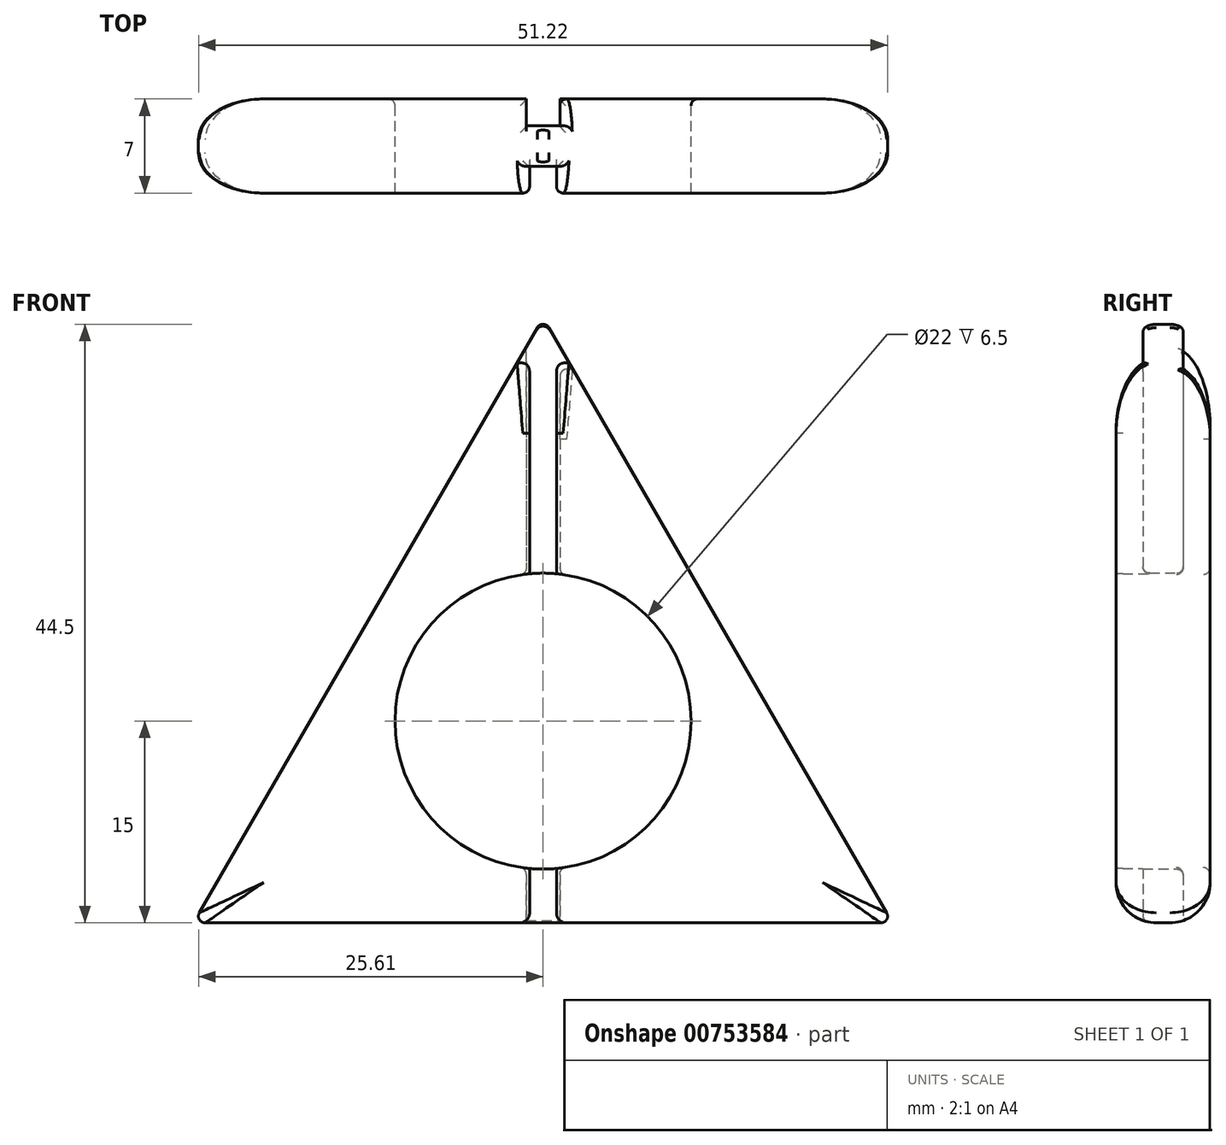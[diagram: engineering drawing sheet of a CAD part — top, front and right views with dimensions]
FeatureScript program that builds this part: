
annotation { "Feature Type Name" : "Feature", "Feature Type Description" : "" }
export const myFeature = defineFeature(function(context is Context, id is Id, definition is map)
    precondition{}
    {
        {
            var Q0;
            Q0=qCreatedBy(makeId("Front.planeOp"),FACE);
            var sketch = newSketch(context, id + "F0", { "sketchPlane" : qUnion([Q0])});
            skPoint(sketch, "E0.center", {"position": v(0, 0) * mm});
            skLineSegment(sketch, "E1", {"start": v(0, 30) * mm, "end": v(-25.98, -15) * mm});
            skLineSegment(sketch, "E2", {"start": v(25.98, -15) * mm, "end": v(-25.98, -15) * mm});
            skLineSegment(sketch, "E3", {"start": v(25.98, -15) * mm, "end": v(0, 30) * mm});
            skCircle(sketch, "E4", {"center": v(0, 0) * mm, "radius": 11 * mm});
            skLineSegment(sketch, "E5", {"start": v(0, 11) * mm, "end": v(0, 30) * mm});
            skSolve(sketch);
        }
        {
            var Q0;
            Q0=makeQuery(id+"F0.imprint","IMPRINT",FACE,{"disambiguationData":[TD([[makeQuery(id+"F0.imprint","IMPRINT",EDGE,{"derivedFrom":sQuery(id+"F0.wireOp",EDGE,"E1")}),1.0]])]});
            extrude(context, id + "F1", {"entities" : qUnion([Q0]), "depth" : 7 * mm, "offsetDistance" : 25.4 * mm});
        }
        {
            var Q0;
            Q0=qCreatedBy(makeId("Front.planeOp"),FACE);
            var sketch = newSketch(context, id + "F2", { "sketchPlane" : qUnion([Q0])});
            skLineSegment(sketch, "E6", {"start": v(-1.25, 30.57) * mm, "end": v(-1.25, 19.34) * mm});
            skLineSegment(sketch, "E7", {"start": v(-1.25, 36.4) * mm, "end": v(-1.25, 9.77) * mm});
            skLineSegment(sketch, "E8.MirrorCS", {"start": v(1.25, 36.4) * mm, "end": v(1.25, 9.77) * mm});
            skLineSegment(sketch, "E9", {"start": v(-1.25, 36.4) * mm, "end": v(1.25, 36.4) * mm});
            skLineSegment(sketch, "E10", {"start": v(-1.25, 9.77) * mm, "end": v(1.25, 9.77) * mm});
            skArc(sketch, "E11", {"start": v(1.25, 10.92) * mm, "mid": v(0, 11) * mm, "end": v(-1.25, 10.92) * mm});
            skLineSegment(sketch, "E12", {"start": v(-1.25, 27.85) * mm, "end": v(0, 30) * mm});
            skLineSegment(sketch, "E13", {"start": v(0, 30) * mm, "end": v(1.25, 27.84) * mm});
            skLineSegment(sketch, "E14", {"start": v(1.25, -10.91) * mm, "end": v(1.25, -15) * mm});
            skLineSegment(sketch, "E15.MirrorCS", {"start": v(-1.25, -10.91) * mm, "end": v(-1.25, -15) * mm});
            skLineSegment(sketch, "E16", {"start": v(1.25, -15) * mm, "end": v(-1.25, -15) * mm});
            skLineSegment(sketch, "E17", {"start": v(1.25, -10.91) * mm, "end": v(-1.25, -10.91) * mm});
            skSolve(sketch);
        }
        {
            var Q0;
            Q0 = qSketchRegion(id + "F2", true);
            extrude(context, id + "F3", {"entities" : qUnion([Q0]), "operationType" : NewBodyOperationType.REMOVE, "oppositeDirection" : true, "depth" : -2 * mm, "offsetDistance" : 25.4 * mm});
        }
        {
            var Q0;
            Q0=makeQuery(id+"F1.opExtrude","CAP_EDGE",EDGE,{"disambiguationData":[OSD([sQuery(id+"F0.wireOp",EDGE,"E3")])],"isStart":true});
            var Q1;
            Q1=makeQuery(id+"F1.opExtrude","CAP_EDGE",EDGE,{"disambiguationData":[OSD([sQuery(id+"F0.wireOp",EDGE,"E3")])],"isStart":false});
            var Q2;
            Q2=makeQuery(id+"F1.opExtrude","CAP_EDGE",EDGE,{"disambiguationData":[OSD([sQuery(id+"F0.wireOp",EDGE,"E1")])],"isStart":true});
            var Q3;
            {var subQ0=sQuery(id+"F0.wireOp",EDGE,"E1");var subQ1=sQuery(id+"F0.wireOp",EDGE,"E2");Q3=makeQuery(id+"F3.boolean.opBoolean","SPLIT",EDGE,{"disambiguationData":[TD([makeQuery(id+"F1.opExtrude","SWEPT_FACE",FACE,{"disambiguationData":[OSD([subQ0])]})])],"derivedFrom":makeQuery(id+"F1.opExtrude","CAP_EDGE",EDGE,{"disambiguationData":[OSD([subQ1])],"isStart":true})});}
            var Q4;
            Q4=makeQuery(id+"F1.opExtrude","CAP_EDGE",EDGE,{"disambiguationData":[OSD([sQuery(id+"F0.wireOp",EDGE,"E2")])],"isStart":false});
            var Q5;
            {var subQ0=sQuery(id+"F0.wireOp",EDGE,"E3");var subQ1=sQuery(id+"F0.wireOp",EDGE,"E2");Q5=makeQuery(id+"F3.boolean.opBoolean","SPLIT",EDGE,{"disambiguationData":[TD([makeQuery(id+"F1.opExtrude","SWEPT_FACE",FACE,{"disambiguationData":[OSD([subQ0])]})])],"derivedFrom":makeQuery(id+"F1.opExtrude","CAP_EDGE",EDGE,{"disambiguationData":[OSD([subQ1])],"isStart":true})});}
            var Q6;
            Q6=makeQuery(id+"F1.opExtrude","CAP_EDGE",EDGE,{"disambiguationData":[OSD([sQuery(id+"F0.wireOp",EDGE,"E1")])],"isStart":false});
            fillet(context, id + "F4", {"entities" : qUnion([Q0, Q1, Q2, Q3, Q4, Q5, Q6]), "radius" : 3 * mm, "tangentPropagation" : true, "allowEdgeOverflow" : false});
        }
        {
            var Q0;
            {var subQ0=sQuery(id+"F0.wireOp",EDGE,"E4");Q0=makeQuery(id+"F3.boolean.opBoolean","SPLIT",EDGE,{"disambiguationData":[TD([makeQuery(id+"F3.opExtrude","SWEPT_FACE",FACE,{"disambiguationData":[OSD([sQuery(id+"F2.wireOp",EDGE,"E7")])]})])],"derivedFrom":makeQuery(id+"F1.opExtrude","CAP_EDGE",EDGE,{"disambiguationData":[OSD([subQ0])],"isStart":true})});}
            var Q1;
            {var subQ0=sQuery(id+"F0.wireOp",EDGE,"E4");Q1=makeQuery(id+"F3.boolean.opBoolean","SPLIT",EDGE,{"disambiguationData":[TD([makeQuery(id+"F3.opExtrude","SWEPT_FACE",FACE,{"disambiguationData":[OSD([sQuery(id+"F2.wireOp",EDGE,"E8.MirrorCS")])]})])],"derivedFrom":makeQuery(id+"F1.opExtrude","CAP_EDGE",EDGE,{"disambiguationData":[OSD([subQ0])],"isStart":true})});}
            var Q2;
            Q2=makeQuery(id+"F3.boolean.opBoolean","INTERSECT",EDGE,{"derivedFrom":[makeQuery(id+"F1.opExtrude","SWEPT_FACE",FACE,{"disambiguationData":[OSD([sQuery(id+"F0.wireOp",EDGE,"E4")])]}),makeQuery(id+"F3.opExtrude","SWEPT_FACE",FACE,{"disambiguationData":[OSD([sQuery(id+"F2.wireOp",EDGE,"E15.MirrorCS")])]})]});
            var Q3;
            Q3=makeQuery(id+"F3.boolean.opBoolean","INTERSECT",EDGE,{"derivedFrom":[makeQuery(id+"F1.opExtrude","SWEPT_FACE",FACE,{"disambiguationData":[OSD([sQuery(id+"F0.wireOp",EDGE,"E4")])]}),makeQuery(id+"F3.opExtrude","SWEPT_FACE",FACE,{"disambiguationData":[OSD([sQuery(id+"F2.wireOp",EDGE,"E14")])]})]});
            var Q4;
            Q4=makeQuery(id+"F3.boolean.opBoolean","INTERSECT",EDGE,{"derivedFrom":[makeQuery(id+"F1.opExtrude","SWEPT_FACE",FACE,{"disambiguationData":[OSD([sQuery(id+"F0.wireOp",EDGE,"E4")])]}),makeQuery(id+"F3.opExtrude","CAP_FACE",FACE,{"disambiguationData":[OSD([sQuery(id+"F2.wireOp",EDGE,"E14"),sQuery(id+"F2.wireOp",EDGE,"E15.MirrorCS"),sQuery(id+"F2.wireOp",EDGE,"E16"),sQuery(id+"F2.wireOp",EDGE,"E17")])],"isStart":false})]});
            var Q5;
            {var subQ0=sQuery(id+"F2.wireOp",EDGE,"E14");var subQ1=sQuery(id+"F0.wireOp",EDGE,"E3");var subQ2=sQuery(id+"F0.wireOp",EDGE,"E2");Q5=makeQuery(id+"F4.opFillet","BLEND_EDGE",EDGE,{"blendedFrom":[makeQuery(id+"F3.boolean.opBoolean","SPLIT",EDGE,{"disambiguationData":[TD([makeQuery(id+"F1.opExtrude","SWEPT_FACE",FACE,{"disambiguationData":[OSD([subQ1])]})])],"derivedFrom":makeQuery(id+"F1.opExtrude","CAP_EDGE",EDGE,{"disambiguationData":[OSD([subQ2])],"isStart":true})}),makeQuery(id+"F3.boolean.opBoolean","COPY",FACE,{"derivedFrom":makeQuery(id+"F3.opExtrude","CAP_FACE",FACE,{"disambiguationData":[OSD([subQ0,sQuery(id+"F2.wireOp",EDGE,"E15.MirrorCS"),sQuery(id+"F2.wireOp",EDGE,"E16"),sQuery(id+"F2.wireOp",EDGE,"E17")])],"isStart":false})})],"blendedInto":[makeQuery(id+"F3.boolean.opBoolean","COPY",FACE,{"derivedFrom":makeQuery(id+"F3.opExtrude","CAP_FACE",FACE,{"disambiguationData":[OSD([subQ0,sQuery(id+"F2.wireOp",EDGE,"E15.MirrorCS"),sQuery(id+"F2.wireOp",EDGE,"E16"),sQuery(id+"F2.wireOp",EDGE,"E17")])],"isStart":false})})]});}
            var Q6;
            {var subQ0=sQuery(id+"F0.wireOp",EDGE,"E3");var subQ1=sQuery(id+"F0.wireOp",EDGE,"E2");Q6=makeQuery(id+"F4.opFillet","BLEND_EDGE",EDGE,{"blendedFrom":[makeQuery(id+"F3.boolean.opBoolean","SPLIT",EDGE,{"disambiguationData":[TD([makeQuery(id+"F1.opExtrude","SWEPT_FACE",FACE,{"disambiguationData":[OSD([subQ0])]})])],"derivedFrom":makeQuery(id+"F1.opExtrude","CAP_EDGE",EDGE,{"disambiguationData":[OSD([subQ1])],"isStart":true})}),makeQuery(id+"F3.boolean.opBoolean","COPY",FACE,{"derivedFrom":makeQuery(id+"F3.opExtrude","SWEPT_FACE",FACE,{"disambiguationData":[OSD([sQuery(id+"F2.wireOp",EDGE,"E15.MirrorCS")])]})})],"blendedInto":[makeQuery(id+"F3.boolean.opBoolean","COPY",FACE,{"derivedFrom":makeQuery(id+"F3.opExtrude","SWEPT_FACE",FACE,{"disambiguationData":[OSD([sQuery(id+"F2.wireOp",EDGE,"E15.MirrorCS")])]})})]});}
            var Q7;
            {var subQ0=makeQuery(id+"F3.opExtrude","SWEPT_FACE",FACE,{"disambiguationData":[OSD([sQuery(id+"F2.wireOp",EDGE,"E14")])]});var subQ1=sQuery(id+"F0.wireOp",EDGE,"E3");var subQ2=sQuery(id+"F0.wireOp",EDGE,"E2");Q7=makeQuery(id+"F4.opFillet","BLEND_EDGE",EDGE,{"blendedFrom":[makeQuery(id+"F3.boolean.opBoolean","SPLIT",EDGE,{"disambiguationData":[TD([makeQuery(id+"F1.opExtrude","SWEPT_FACE",FACE,{"disambiguationData":[OSD([subQ1])]})])],"derivedFrom":makeQuery(id+"F1.opExtrude","CAP_EDGE",EDGE,{"disambiguationData":[OSD([subQ2])],"isStart":true})}),makeQuery(id+"F3.boolean.opBoolean","COPY",FACE,{"derivedFrom":subQ0})],"blendedInto":[makeQuery(id+"F3.boolean.opBoolean","COPY",FACE,{"derivedFrom":subQ0})]});}
            var Q8;
            Q8=makeQuery(id+"F3.boolean.opBoolean","INTERSECT",EDGE,{"derivedFrom":[makeQuery(id+"F1.opExtrude","SWEPT_FACE",FACE,{"disambiguationData":[OSD([sQuery(id+"F0.wireOp",EDGE,"E4")])]}),makeQuery(id+"F3.opExtrude","CAP_FACE",FACE,{"disambiguationData":[OSD([sQuery(id+"F2.wireOp",EDGE,"E7"),sQuery(id+"F2.wireOp",EDGE,"E8.MirrorCS"),sQuery(id+"F2.wireOp",EDGE,"E9"),sQuery(id+"F2.wireOp",EDGE,"E10")])],"isStart":false})]});
            var Q9;
            Q9=makeQuery(id+"F3.boolean.opBoolean","INTERSECT",EDGE,{"derivedFrom":[makeQuery(id+"F1.opExtrude","SWEPT_FACE",FACE,{"disambiguationData":[OSD([sQuery(id+"F0.wireOp",EDGE,"E4")])]}),makeQuery(id+"F3.opExtrude","SWEPT_FACE",FACE,{"disambiguationData":[OSD([sQuery(id+"F2.wireOp",EDGE,"E7")])]})]});
            var Q10;
            Q10=makeQuery(id+"F3.boolean.opBoolean","INTERSECT",EDGE,{"derivedFrom":[makeQuery(id+"F1.opExtrude","SWEPT_FACE",FACE,{"disambiguationData":[OSD([sQuery(id+"F0.wireOp",EDGE,"E4")])]}),makeQuery(id+"F3.opExtrude","SWEPT_FACE",FACE,{"disambiguationData":[OSD([sQuery(id+"F2.wireOp",EDGE,"E8.MirrorCS")])]})]});
            var Q11;
            Q11=makeQuery(id+"F3.boolean.opBoolean","COPY",EDGE,{"derivedFrom":makeQuery(id+"F3.opExtrude","CAP_EDGE",EDGE,{"disambiguationData":[OSD([sQuery(id+"F2.wireOp",EDGE,"E7")])],"isStart":true})});
            var Q12;
            Q12=makeQuery(id+"F3.boolean.opBoolean","COPY",EDGE,{"derivedFrom":makeQuery(id+"F3.opExtrude","CAP_EDGE",EDGE,{"disambiguationData":[OSD([sQuery(id+"F2.wireOp",EDGE,"E8.MirrorCS")])],"isStart":true})});
            var Q13;
            Q13=makeQuery(id+"F4.opFillet","BLEND_EDGE",EDGE,{"blendedFrom":[makeQuery(id+"F1.opExtrude","CAP_EDGE",EDGE,{"disambiguationData":[OSD([sQuery(id+"F0.wireOp",EDGE,"E3")])],"isStart":true}),makeQuery(id+"F3.boolean.opBoolean","COPY",FACE,{"derivedFrom":makeQuery(id+"F3.opExtrude","CAP_FACE",FACE,{"disambiguationData":[OSD([sQuery(id+"F2.wireOp",EDGE,"E7"),sQuery(id+"F2.wireOp",EDGE,"E8.MirrorCS"),sQuery(id+"F2.wireOp",EDGE,"E9"),sQuery(id+"F2.wireOp",EDGE,"E10")])],"isStart":false})})],"blendedInto":[makeQuery(id+"F3.boolean.opBoolean","COPY",FACE,{"derivedFrom":makeQuery(id+"F3.opExtrude","CAP_FACE",FACE,{"disambiguationData":[OSD([sQuery(id+"F2.wireOp",EDGE,"E7"),sQuery(id+"F2.wireOp",EDGE,"E8.MirrorCS"),sQuery(id+"F2.wireOp",EDGE,"E9"),sQuery(id+"F2.wireOp",EDGE,"E10")])],"isStart":false})})]});
            var Q14;
            Q14=makeQuery(id+"F4.opFillet","BLEND_EDGE",EDGE,{"blendedFrom":[makeQuery(id+"F1.opExtrude","CAP_EDGE",EDGE,{"disambiguationData":[OSD([sQuery(id+"F0.wireOp",EDGE,"E1")])],"isStart":true}),makeQuery(id+"F3.boolean.opBoolean","COPY",FACE,{"derivedFrom":makeQuery(id+"F3.opExtrude","CAP_FACE",FACE,{"disambiguationData":[OSD([sQuery(id+"F2.wireOp",EDGE,"E7"),sQuery(id+"F2.wireOp",EDGE,"E8.MirrorCS"),sQuery(id+"F2.wireOp",EDGE,"E9"),sQuery(id+"F2.wireOp",EDGE,"E10")])],"isStart":false})})],"blendedInto":[makeQuery(id+"F3.boolean.opBoolean","COPY",FACE,{"derivedFrom":makeQuery(id+"F3.opExtrude","CAP_FACE",FACE,{"disambiguationData":[OSD([sQuery(id+"F2.wireOp",EDGE,"E7"),sQuery(id+"F2.wireOp",EDGE,"E8.MirrorCS"),sQuery(id+"F2.wireOp",EDGE,"E9"),sQuery(id+"F2.wireOp",EDGE,"E10")])],"isStart":false})})]});
            var Q15;
            Q15=makeQuery(id+"F1.opExtrude","SWEPT_EDGE",EDGE,{"disambiguationData":[OSD([sQuery(id+"F0.wireOp",EDGE,"E1"),sQuery(id+"F0.wireOp",EDGE,"E3")])]});
            var Q16;
            Q16=makeQuery(id+"F1.opExtrude","SWEPT_EDGE",EDGE,{"disambiguationData":[OSD([sQuery(id+"F0.wireOp",EDGE,"E1"),sQuery(id+"F0.wireOp",EDGE,"E2")])]});
            var Q17;
            Q17=makeQuery(id+"F1.opExtrude","SWEPT_EDGE",EDGE,{"disambiguationData":[OSD([sQuery(id+"F0.wireOp",EDGE,"E2"),sQuery(id+"F0.wireOp",EDGE,"E3")])]});
            fillet(context, id + "F5", {"entities" : qUnion([Q0, Q1, Q2, Q3, Q4, Q5, Q6, Q7, Q8, Q9, Q10, Q11, Q12, Q13, Q14, Q15, Q16, Q17]), "radius" : .5 * mm, "tangentPropagation" : true, "allowEdgeOverflow" : false});
        }
        {
            var Q0;
            Q0=qCreatedBy(makeId("Front.planeOp"),FACE);
            cPlane(context, id + "F6", {"entities" : qUnion([Q0]), "cplaneType" : CPlaneType.OFFSET, "offset" : 7 * mm, "width" : 152.4 * mm, "height" : 152.4 * mm});
        }
        {
            var Q0;
            Q0=qCreatedBy(id+"F6.planeOp",FACE);
            var sketch = newSketch(context, id + "F7", { "sketchPlane" : qUnion([Q0])});
            skLineSegment(sketch, "E18", {"start": v(-1, 20.28) * mm, "end": v(-1, -3.7) * mm});
            skLineSegment(sketch, "E19", {"start": v(-1, 49.73) * mm, "end": v(-1, -21.55) * mm});
            skLineSegment(sketch, "E20.MirrorCS", {"start": v(1, 49.73) * mm, "end": v(1, -21.55) * mm});
            skLineSegment(sketch, "E21", {"start": v(-1, 49.73) * mm, "end": v(1, 49.73) * mm});
            skLineSegment(sketch, "E22", {"start": v(-1, -21.55) * mm, "end": v(1, -21.55) * mm});
            skSolve(sketch);
        }
        {
            var Q0;
            Q0=makeQuery(id+"F7.imprint","IMPRINT",FACE,{"disambiguationData":[TD([[makeQuery(id+"F7.imprint","IMPRINT",EDGE,{"derivedFrom":sQuery(id+"F7.wireOp",EDGE,"E20.MirrorCS")}),-1.0]])]});
            extrude(context, id + "F8", {"entities" : qUnion([Q0]), "operationType" : NewBodyOperationType.REMOVE, "oppositeDirection" : true, "depth" : 2 * mm, "offsetDistance" : 25.4 * mm});
        }
        {
            var Q0;
            {var subQ0=sQuery(id+"F0.wireOp",EDGE,"E1");Q0=makeQuery(id+"F8.boolean.opBoolean","INTERSECT",EDGE,{"derivedFrom":[makeQuery(id+"F4.opFillet","BLEND_FACE",FACE,{"disambiguationData":[OSD([subQ0]),TDD([makeQuery(id+"F1.opExtrude","CAP_EDGE",EDGE,{"disambiguationData":[OSD([subQ0])],"isStart":false})])]}),makeQuery(id+"F8.opExtrude","SWEPT_FACE",FACE,{"disambiguationData":[OSD([sQuery(id+"F7.wireOp",EDGE,"E19")])]})]});}
            var Q1;
            {var subQ0=sQuery(id+"F0.wireOp",EDGE,"E3");Q1=makeQuery(id+"F8.boolean.opBoolean","INTERSECT",EDGE,{"derivedFrom":[makeQuery(id+"F4.opFillet","BLEND_FACE",FACE,{"disambiguationData":[OSD([subQ0]),TDD([makeQuery(id+"F1.opExtrude","CAP_EDGE",EDGE,{"disambiguationData":[OSD([subQ0])],"isStart":false})])]}),makeQuery(id+"F8.opExtrude","SWEPT_FACE",FACE,{"disambiguationData":[OSD([sQuery(id+"F7.wireOp",EDGE,"E20.MirrorCS")])]})]});}
            var Q2;
            {var subQ1=sQuery(id+"F0.wireOp",EDGE,"E1");var subQ2=sQuery(id+"F7.wireOp",EDGE,"E19");Q2=makeQuery(id+"F8.boolean.opBoolean","COPY",EDGE,{"disambiguationData":[TD([makeQuery(id+"F4.opFillet","BLEND_FACE",FACE,{"disambiguationData":[OSD([subQ1]),TDD([makeQuery(id+"F1.opExtrude","CAP_EDGE",EDGE,{"disambiguationData":[OSD([subQ1])],"isStart":false})])]})])],"derivedFrom":makeQuery(id+"F8.opExtrude","CAP_EDGE",EDGE,{"disambiguationData":[OSD([subQ2])],"isStart":true})});}
            var Q3;
            {var subQ1=sQuery(id+"F0.wireOp",EDGE,"E3");var subQ2=sQuery(id+"F7.wireOp",EDGE,"E20.MirrorCS");Q3=makeQuery(id+"F8.boolean.opBoolean","COPY",EDGE,{"disambiguationData":[TD([makeQuery(id+"F4.opFillet","BLEND_FACE",FACE,{"disambiguationData":[OSD([subQ1]),TDD([makeQuery(id+"F1.opExtrude","CAP_EDGE",EDGE,{"disambiguationData":[OSD([subQ1])],"isStart":false})])]})])],"derivedFrom":makeQuery(id+"F8.opExtrude","CAP_EDGE",EDGE,{"disambiguationData":[OSD([subQ2])],"isStart":true})});}
            var Q4;
            {var subQ0=sQuery(id+"F0.wireOp",EDGE,"E3");Q4=makeQuery(id+"F8.boolean.opBoolean","INTERSECT",EDGE,{"derivedFrom":[makeQuery(id+"F4.opFillet","BLEND_FACE",FACE,{"disambiguationData":[OSD([subQ0]),TDD([makeQuery(id+"F1.opExtrude","CAP_EDGE",EDGE,{"disambiguationData":[OSD([subQ0])],"isStart":false})])]}),makeQuery(id+"F8.opExtrude","CAP_FACE",FACE,{"disambiguationData":[OSD([sQuery(id+"F7.wireOp",EDGE,"E19"),sQuery(id+"F7.wireOp",EDGE,"E20.MirrorCS"),sQuery(id+"F7.wireOp",EDGE,"E21"),sQuery(id+"F7.wireOp",EDGE,"E22")])],"isStart":false})]});}
            var Q5;
            {var subQ0=sQuery(id+"F0.wireOp",EDGE,"E1");Q5=makeQuery(id+"F8.boolean.opBoolean","INTERSECT",EDGE,{"derivedFrom":[makeQuery(id+"F4.opFillet","BLEND_FACE",FACE,{"disambiguationData":[OSD([subQ0]),TDD([makeQuery(id+"F1.opExtrude","CAP_EDGE",EDGE,{"disambiguationData":[OSD([subQ0])],"isStart":false})])]}),makeQuery(id+"F8.opExtrude","CAP_FACE",FACE,{"disambiguationData":[OSD([sQuery(id+"F7.wireOp",EDGE,"E19"),sQuery(id+"F7.wireOp",EDGE,"E20.MirrorCS"),sQuery(id+"F7.wireOp",EDGE,"E21"),sQuery(id+"F7.wireOp",EDGE,"E22")])],"isStart":false})]});}
            var Q6;
            Q6=makeQuery(id+"F8.boolean.opBoolean","INTERSECT",EDGE,{"disambiguationData":[OD(0.0)],"derivedFrom":[makeQuery(id+"F1.opExtrude","SWEPT_FACE",FACE,{"disambiguationData":[OSD([sQuery(id+"F0.wireOp",EDGE,"E4")])]}),makeQuery(id+"F8.opExtrude","CAP_FACE",FACE,{"disambiguationData":[OSD([sQuery(id+"F7.wireOp",EDGE,"E19"),sQuery(id+"F7.wireOp",EDGE,"E20.MirrorCS"),sQuery(id+"F7.wireOp",EDGE,"E21"),sQuery(id+"F7.wireOp",EDGE,"E22")])],"isStart":false})]});
            var Q7;
            {var subQ1=sQuery(id+"F0.wireOp",EDGE,"E2");var subQ2=sQuery(id+"F7.wireOp",EDGE,"E20.MirrorCS");Q7=makeQuery(id+"F8.boolean.opBoolean","COPY",EDGE,{"disambiguationData":[TD([makeQuery(id+"F4.opFillet","BLEND_FACE",FACE,{"disambiguationData":[OSD([subQ1]),TDD([makeQuery(id+"F1.opExtrude","CAP_EDGE",EDGE,{"disambiguationData":[OSD([subQ1])],"isStart":false})])]})])],"derivedFrom":makeQuery(id+"F8.opExtrude","CAP_EDGE",EDGE,{"disambiguationData":[OSD([subQ2])],"isStart":true})});}
            var Q8;
            {var subQ1=sQuery(id+"F0.wireOp",EDGE,"E2");var subQ2=sQuery(id+"F7.wireOp",EDGE,"E19");Q8=makeQuery(id+"F8.boolean.opBoolean","COPY",EDGE,{"disambiguationData":[TD([makeQuery(id+"F4.opFillet","BLEND_FACE",FACE,{"disambiguationData":[OSD([subQ1]),TDD([makeQuery(id+"F1.opExtrude","CAP_EDGE",EDGE,{"disambiguationData":[OSD([subQ1])],"isStart":false})])]})])],"derivedFrom":makeQuery(id+"F8.opExtrude","CAP_EDGE",EDGE,{"disambiguationData":[OSD([subQ2])],"isStart":true})});}
            var Q9;
            {var subQ0=sQuery(id+"F0.wireOp",EDGE,"E2");Q9=makeQuery(id+"F8.boolean.opBoolean","INTERSECT",EDGE,{"derivedFrom":[makeQuery(id+"F4.opFillet","BLEND_FACE",FACE,{"disambiguationData":[OSD([subQ0]),TDD([makeQuery(id+"F1.opExtrude","CAP_EDGE",EDGE,{"disambiguationData":[OSD([subQ0])],"isStart":false})])]}),makeQuery(id+"F8.opExtrude","SWEPT_FACE",FACE,{"disambiguationData":[OSD([sQuery(id+"F7.wireOp",EDGE,"E19")])]})]});}
            var Q10;
            {var subQ0=sQuery(id+"F0.wireOp",EDGE,"E2");Q10=makeQuery(id+"F8.boolean.opBoolean","INTERSECT",EDGE,{"derivedFrom":[makeQuery(id+"F4.opFillet","BLEND_FACE",FACE,{"disambiguationData":[OSD([subQ0]),TDD([makeQuery(id+"F1.opExtrude","CAP_EDGE",EDGE,{"disambiguationData":[OSD([subQ0])],"isStart":false})])]}),makeQuery(id+"F8.opExtrude","SWEPT_FACE",FACE,{"disambiguationData":[OSD([sQuery(id+"F7.wireOp",EDGE,"E20.MirrorCS")])]})]});}
            var Q11;
            {var subQ0=sQuery(id+"F0.wireOp",EDGE,"E2");Q11=makeQuery(id+"F8.boolean.opBoolean","INTERSECT",EDGE,{"derivedFrom":[makeQuery(id+"F4.opFillet","BLEND_FACE",FACE,{"disambiguationData":[OSD([subQ0]),TDD([makeQuery(id+"F1.opExtrude","CAP_EDGE",EDGE,{"disambiguationData":[OSD([subQ0])],"isStart":false})])]}),makeQuery(id+"F8.opExtrude","CAP_FACE",FACE,{"disambiguationData":[OSD([sQuery(id+"F7.wireOp",EDGE,"E19"),sQuery(id+"F7.wireOp",EDGE,"E20.MirrorCS"),sQuery(id+"F7.wireOp",EDGE,"E21"),sQuery(id+"F7.wireOp",EDGE,"E22")])],"isStart":false})]});}
            fillet(context, id + "F9", {"entities" : qUnion([Q0, Q1, Q2, Q3, Q4, Q5, Q6, Q7, Q8, Q9, Q10, Q11]), "radius" : .5 * mm, "tangentPropagation" : true, "allowEdgeOverflow" : false});
        }
    });
